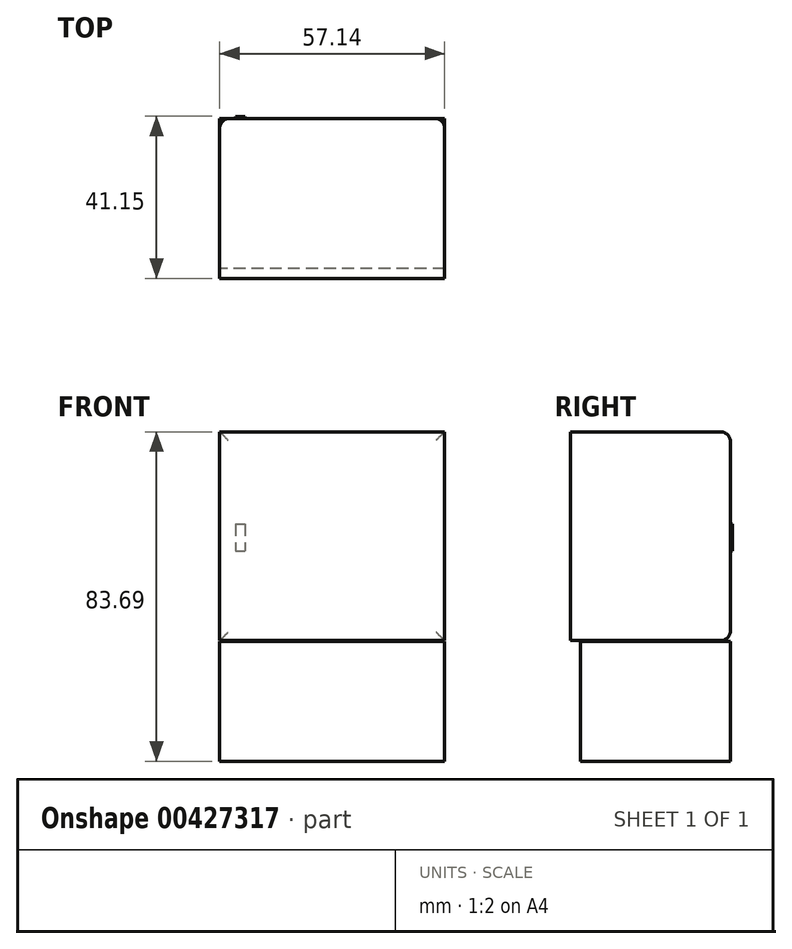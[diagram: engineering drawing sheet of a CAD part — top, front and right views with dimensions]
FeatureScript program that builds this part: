
annotation { "Feature Type Name" : "Feature", "Feature Type Description" : "" }
export const myFeature = defineFeature(function(context is Context, id is Id, definition is map)
    precondition{}
    {
        {
            var Q0;
            Q0=qCreatedBy(makeId("Front.planeOp"),FACE);
            var sketch = newSketch(context, id + "F0", { "sketchPlane" : qUnion([Q0])});
            skLineSegment(sketch, "E0.bottom", {"start": v(28.58, -15.24) * mm, "end": v(-28.57, -15.24) * mm});
            skLineSegment(sketch, "E0.top", {"start": v(28.57, 15.24) * mm, "end": v(-28.58, 15.24) * mm});
            skLineSegment(sketch, "E0.left", {"start": v(28.58, -15.24) * mm, "end": v(28.57, 15.24) * mm});
            skLineSegment(sketch, "E0.right", {"start": v(-28.57, -15.24) * mm, "end": v(-28.58, 15.24) * mm});
            skPoint(sketch, "E0.middle", {"position": v(0, 0) * mm});
            skSolve(sketch);
        }
        {
            var Q0;
            Q0 = qSketchRegion(id + "F0", true);
            extrude(context, id + "F1", {"entities" : qUnion([Q0]), "depth" : 38.1 * mm});
        }
        {
            var Q0;
            Q0=qCreatedBy(makeId("Front.planeOp"),FACE);
            var sketch = newSketch(context, id + "F2", { "sketchPlane" : qUnion([Q0])});
            skLineSegment(sketch, "E1.bottom", {"start": v(28.57, 15.39) * mm, "end": v(-28.57, 15.39) * mm});
            skLineSegment(sketch, "E1.top", {"start": v(28.57, 68.45) * mm, "end": v(-28.57, 68.45) * mm});
            skLineSegment(sketch, "E1.left", {"start": v(28.57, 15.39) * mm, "end": v(28.57, 68.45) * mm});
            skLineSegment(sketch, "E1.right", {"start": v(-28.57, 15.39) * mm, "end": v(-28.57, 68.45) * mm});
            skSolve(sketch);
        }
        {
            var Q0;
            Q0 = qSketchRegion(id + "F2", true);
            extrude(context, id + "F3", {"entities" : qUnion([Q0]), "depth" : 40.64 * mm});
        }
        {
            var Q0;
            Q0=makeQuery(id+"F3.opExtrude","CAP_FACE",FACE,{"disambiguationData":[OSD([sQuery(id+"F2.wireOp",EDGE,"E1.bottom"),sQuery(id+"F2.wireOp",EDGE,"E1.top"),sQuery(id+"F2.wireOp",EDGE,"E1.left"),sQuery(id+"F2.wireOp",EDGE,"E1.right")])],"isStart":true});
            fillet(context, id + "F4", {"entities" : qUnion([Q0]), "radius" : 2.54 * mm, "tangentPropagation" : true, "allowEdgeOverflow" : false});
        }
        {
            var Q0;
            Q0=makeQuery(id+"F3.opExtrude","CAP_FACE",FACE,{"disambiguationData":[OSD([sQuery(id+"F2.wireOp",EDGE,"E1.bottom"),sQuery(id+"F2.wireOp",EDGE,"E1.top"),sQuery(id+"F2.wireOp",EDGE,"E1.left"),sQuery(id+"F2.wireOp",EDGE,"E1.right")])],"isStart":true});
            var sketch = newSketch(context, id + "F5", { "sketchPlane" : qUnion([Q0])});
            skLineSegment(sketch, "E2.bottom", {"start": v(24.49, 44.98) * mm, "end": v(22.1, 44.98) * mm});
            skLineSegment(sketch, "E2.top", {"start": v(24.49, 38.18) * mm, "end": v(22.1, 38.18) * mm});
            skLineSegment(sketch, "E2.left", {"start": v(24.49, 44.98) * mm, "end": v(24.49, 38.18) * mm});
            skLineSegment(sketch, "E2.right", {"start": v(22.1, 44.98) * mm, "end": v(22.1, 38.18) * mm});
            skPoint(sketch, "E2.middle", {"position": v(23.3, 41.58) * mm});
            skSolve(sketch);
        }
        {
            var Q0;
            Q0 = qSketchRegion(id + "F5", true);
            extrude(context, id + "F6", {"entities" : qUnion([Q0]), "operationType" : NewBodyOperationType.ADD, "depth" : 0.5 * mm});
        }
    });
